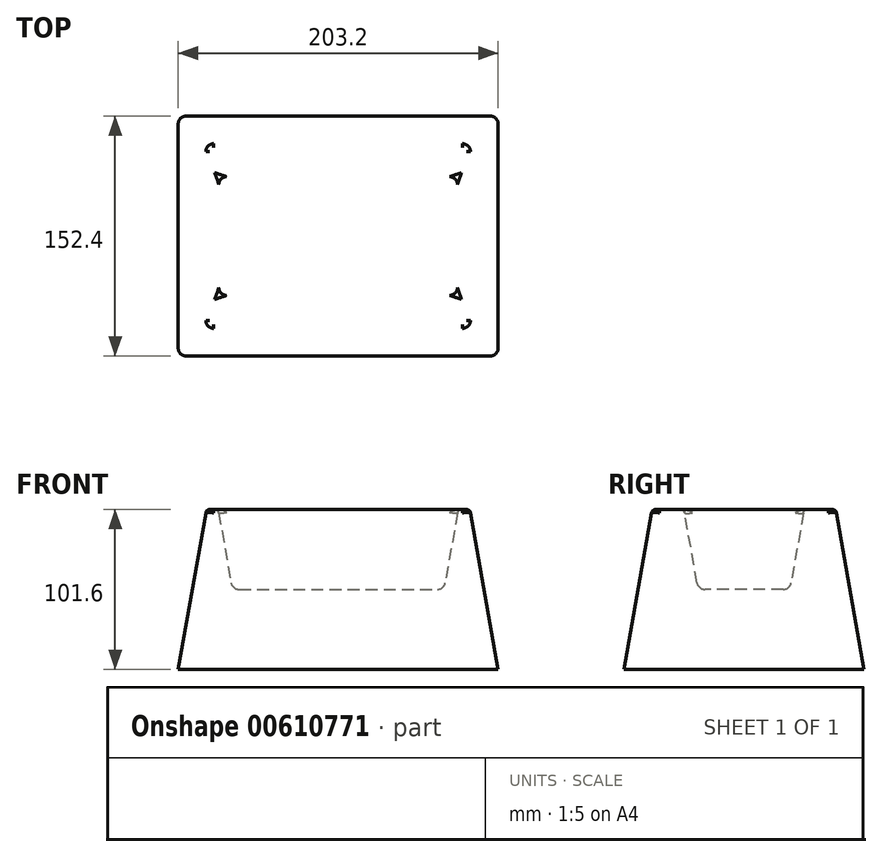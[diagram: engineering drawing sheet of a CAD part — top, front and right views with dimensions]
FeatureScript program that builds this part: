
annotation { "Feature Type Name" : "Feature", "Feature Type Description" : "" }
export const myFeature = defineFeature(function(context is Context, id is Id, definition is map)
    precondition{}
    {
        {
            var Q0;
            Q0=qCreatedBy(makeId("Top.planeOp"),FACE);
            var sketch = newSketch(context, id + "F0", { "sketchPlane" : qUnion([Q0])});
            skLineSegment(sketch, "E0.bottom", {"start": v(101.6, 76.2) * mm, "end": v(-101.6, 76.2) * mm});
            skLineSegment(sketch, "E0.top", {"start": v(101.6, -76.2) * mm, "end": v(-101.6, -76.2) * mm});
            skLineSegment(sketch, "E0.left", {"start": v(101.6, 76.2) * mm, "end": v(101.6, -76.2) * mm});
            skLineSegment(sketch, "E0.right", {"start": v(-101.6, 76.2) * mm, "end": v(-101.6, -76.2) * mm});
            skPoint(sketch, "E0.middle", {"position": v(0, 0) * mm});
            skSolve(sketch);
        }
        {
            var Q0;
            Q0=makeQuery(id+"F0.imprint","IMPRINT",FACE,{"disambiguationData":[TD([[makeQuery(id+"F0.imprint","IMPRINT",EDGE,{"derivedFrom":sQuery(id+"F0.wireOp",EDGE,"E0.bottom")}),1.0]])]});
            extrude(context, id + "F1", {"entities" : qUnion([Q0]), "depth" : 101.6 * mm, "offsetDistance" : 25.4 * mm, "hasDraft" : true, "draftAngle" : 10 * degree, "draftPullDirection" : true});
        }
        {
            var Q0;
            Q0=makeQuery(id+"F1.opExtrude","CAP_FACE",FACE,{"disambiguationData":[OSD([sQuery(id+"F0.wireOp",EDGE,"E0.bottom"),sQuery(id+"F0.wireOp",EDGE,"E0.top"),sQuery(id+"F0.wireOp",EDGE,"E0.left"),sQuery(id+"F0.wireOp",EDGE,"E0.right")])],"isStart":false});
            var sketch = newSketch(context, id + "F2", { "sketchPlane" : qUnion([Q0])});
            skLineSegment(sketch, "E1.bottom", {"start": v(76.2, 38.1) * mm, "end": v(-76.2, 38.1) * mm});
            skLineSegment(sketch, "E1.top", {"start": v(76.2, -38.1) * mm, "end": v(-76.2, -38.1) * mm});
            skLineSegment(sketch, "E1.left", {"start": v(76.2, 38.1) * mm, "end": v(76.2, -38.1) * mm});
            skLineSegment(sketch, "E1.right", {"start": v(-76.2, 38.1) * mm, "end": v(-76.2, -38.1) * mm});
            skPoint(sketch, "E1.middle", {"position": v(0, 0) * mm});
            skSolve(sketch);
        }
        {
            var Q0;
            Q0=makeQuery(id+"F2.imprint","IMPRINT",FACE,{"disambiguationData":[TD([[makeQuery(id+"F2.imprint","IMPRINT",EDGE,{"derivedFrom":sQuery(id+"F2.wireOp",EDGE,"E1.bottom")}),1.0]])]});
            extrude(context, id + "F3", {"entities" : qUnion([Q0]), "operationType" : NewBodyOperationType.REMOVE, "oppositeDirection" : true, "depth" : 50.8 * mm, "offsetDistance" : 25.4 * mm, "hasDraft" : true, "draftAngle" : 10 * degree, "draftPullDirection" : true});
        }
        {
            var Q0;
            Q0=makeQuery(id+"F1.opExtrude","CAP_FACE",FACE,{"disambiguationData":[OSD([sQuery(id+"F0.wireOp",EDGE,"E0.bottom"),sQuery(id+"F0.wireOp",EDGE,"E0.top"),sQuery(id+"F0.wireOp",EDGE,"E0.left"),sQuery(id+"F0.wireOp",EDGE,"E0.right")])],"isStart":false});
            fillet(context, id + "F4", {"entities" : qUnion([Q0]), "radius" : 2.54 * mm, "tangentPropagation" : true, "allowEdgeOverflow" : false});
        }
        {
            var Q0;
            Q0=makeQuery(id+"F1.opExtrude","SWEPT_EDGE",EDGE,{"disambiguationData":[OSD([sQuery(id+"F0.wireOp",EDGE,"E0.bottom"),sQuery(id+"F0.wireOp",EDGE,"E0.right")])]});
            var Q1;
            Q1=makeQuery(id+"F1.opExtrude","SWEPT_EDGE",EDGE,{"disambiguationData":[OSD([sQuery(id+"F0.wireOp",EDGE,"E0.bottom"),sQuery(id+"F0.wireOp",EDGE,"E0.left")])]});
            var Q2;
            Q2=makeQuery(id+"F1.opExtrude","SWEPT_EDGE",EDGE,{"disambiguationData":[OSD([sQuery(id+"F0.wireOp",EDGE,"E0.top"),sQuery(id+"F0.wireOp",EDGE,"E0.left")])]});
            var Q3;
            Q3=makeQuery(id+"F1.opExtrude","SWEPT_EDGE",EDGE,{"disambiguationData":[OSD([sQuery(id+"F0.wireOp",EDGE,"E0.top"),sQuery(id+"F0.wireOp",EDGE,"E0.right")])]});
            var Q4;
            Q4=makeQuery(id+"F3.boolean.opBoolean","COPY",FACE,{"derivedFrom":makeQuery(id+"F3.opExtrude","CAP_FACE",FACE,{"disambiguationData":[OSD([sQuery(id+"F2.wireOp",EDGE,"E1.bottom"),sQuery(id+"F2.wireOp",EDGE,"E1.top"),sQuery(id+"F2.wireOp",EDGE,"E1.left"),sQuery(id+"F2.wireOp",EDGE,"E1.right")])],"isStart":false})});
            var Q5;
            Q5=makeQuery(id+"F3.boolean.opBoolean","COPY",EDGE,{"derivedFrom":makeQuery(id+"F3.opExtrude","SWEPT_EDGE",EDGE,{"disambiguationData":[OSD([sQuery(id+"F2.wireOp",EDGE,"E1.bottom"),sQuery(id+"F2.wireOp",EDGE,"E1.right")])]})});
            var Q6;
            Q6=makeQuery(id+"F3.boolean.opBoolean","COPY",EDGE,{"derivedFrom":makeQuery(id+"F3.opExtrude","SWEPT_EDGE",EDGE,{"disambiguationData":[OSD([sQuery(id+"F2.wireOp",EDGE,"E1.bottom"),sQuery(id+"F2.wireOp",EDGE,"E1.left")])]})});
            var Q7;
            Q7=makeQuery(id+"F3.boolean.opBoolean","COPY",EDGE,{"derivedFrom":makeQuery(id+"F3.opExtrude","SWEPT_EDGE",EDGE,{"disambiguationData":[OSD([sQuery(id+"F2.wireOp",EDGE,"E1.top"),sQuery(id+"F2.wireOp",EDGE,"E1.left")])]})});
            var Q8;
            Q8=makeQuery(id+"F3.boolean.opBoolean","COPY",EDGE,{"derivedFrom":makeQuery(id+"F3.opExtrude","SWEPT_EDGE",EDGE,{"disambiguationData":[OSD([sQuery(id+"F2.wireOp",EDGE,"E1.top"),sQuery(id+"F2.wireOp",EDGE,"E1.right")])]})});
            fillet(context, id + "F5", {"entities" : qUnion([Q0, Q1, Q2, Q3, Q4, Q5, Q6, Q7, Q8]), "radius" : 5.08 * mm, "tangentPropagation" : true, "allowEdgeOverflow" : false});
        }
    });
